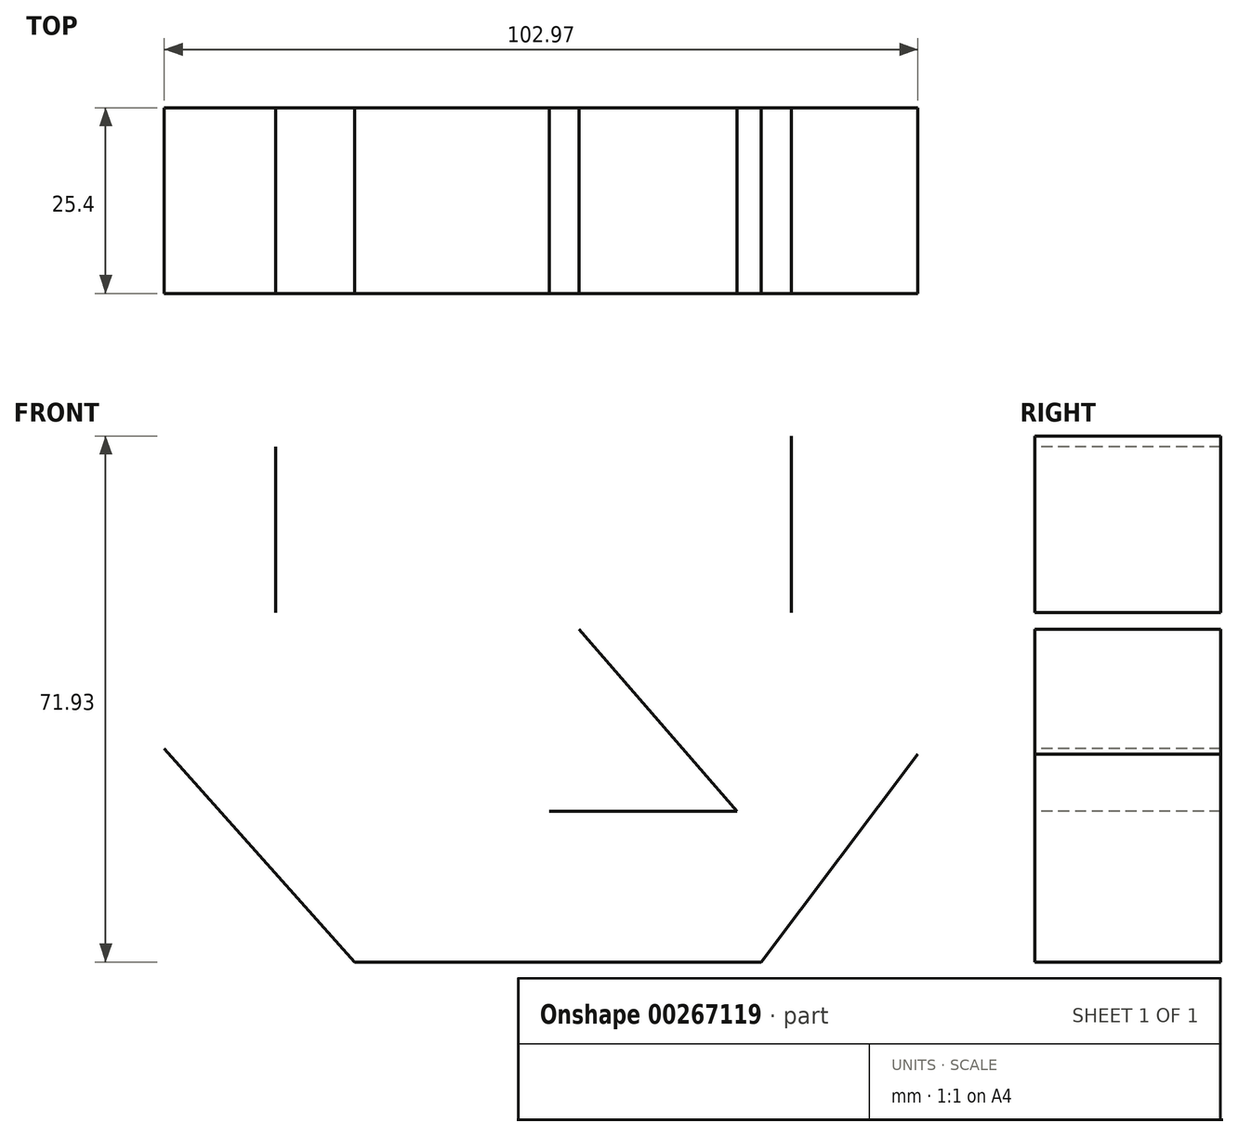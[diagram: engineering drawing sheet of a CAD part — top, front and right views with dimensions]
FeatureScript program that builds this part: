
annotation { "Feature Type Name" : "Feature", "Feature Type Description" : "" }
export const myFeature = defineFeature(function(context is Context, id is Id, definition is map)
    precondition{}
    {
        {
            var Q0;
            Q0=qCreatedBy(makeId("Front.planeOp"),FACE);
            var sketch = newSketch(context, id + "F0", { "sketchPlane" : qUnion([Q0])});
            skLineSegment(sketch, "E0", {"start": v(-37.36, 44.14) * mm, "end": v(-37.36, 21.47) * mm});
            skLineSegment(sketch, "E1", {"start": v(33.08, 45.63) * mm, "end": v(33.08, 21.47) * mm});
            skLineSegment(sketch, "E2", {"start": v(33.08, 45.63) * mm, "end": v(33.08, 44.14) * mm});
            skLineSegment(sketch, "E3", {"start": v(-52.6, 2.88) * mm, "end": v(-26.58, -26.3) * mm});
            skLineSegment(sketch, "E4", {"start": v(-26.58, -26.3) * mm, "end": v(29, -26.3) * mm});
            skLineSegment(sketch, "E5", {"start": v(29, -26.3) * mm, "end": v(50.37, 2.14) * mm});
            skLineSegment(sketch, "E6", {"start": v(4.09, 19.24) * mm, "end": v(25.65, -5.67) * mm});
            skLineSegment(sketch, "E7", {"start": v(25.65, -5.67) * mm, "end": v(0, -5.67) * mm});
            skSolve(sketch);
        }
        {
            var Q0;
            Q0 = qSketchRegion(id + "F0", true);
            var Q1;
            Q1=sQuery(id+"F0.wireOp",EDGE,"E0");
            var Q2;
            Q2=sQuery(id+"F0.wireOp",EDGE,"E1");
            var Q3;
            Q3=sQuery(id+"F0.wireOp",EDGE,"E6");
            var Q4;
            Q4=sQuery(id+"F0.wireOp",EDGE,"E7");
            var Q5;
            Q5=sQuery(id+"F0.wireOp",EDGE,"E3");
            var Q6;
            Q6=sQuery(id+"F0.wireOp",EDGE,"E4");
            var Q7;
            Q7=sQuery(id+"F0.wireOp",EDGE,"E5");
            extrude(context, id + "F1", {"entities" : qUnion([Q0]), "bodyType" : ToolBodyType.SURFACE, "surfaceEntities" : qUnion([Q1, Q2, Q3, Q4, Q5, Q6, Q7]), "depth" : 25.4 * mm});
        }
    });
